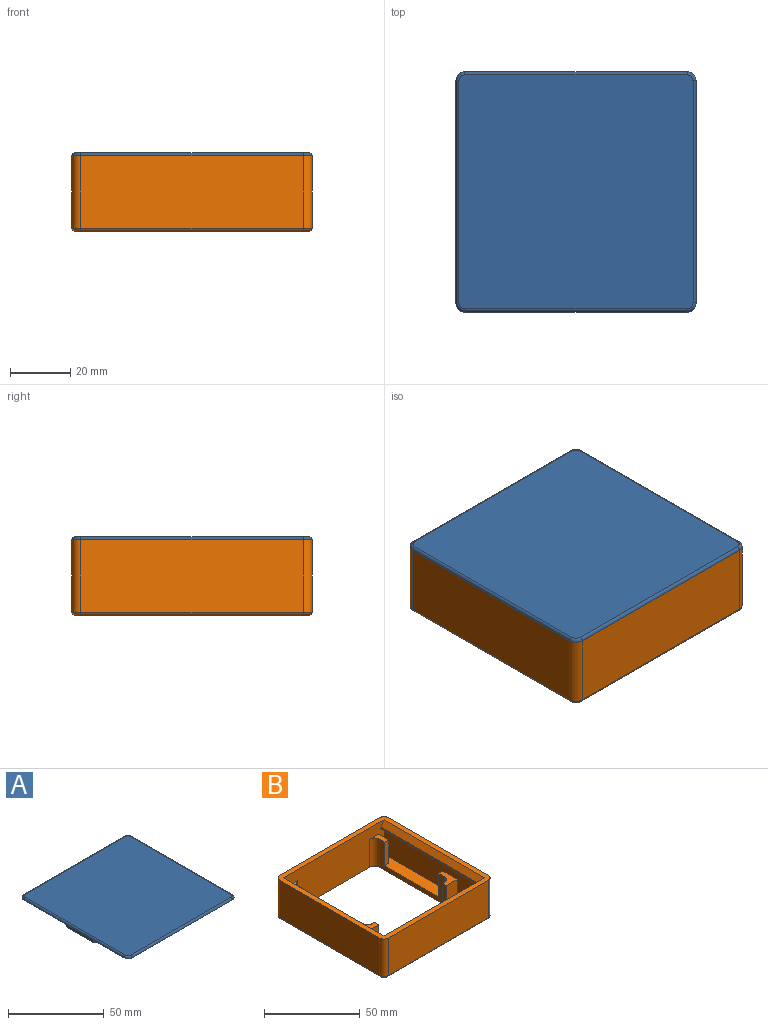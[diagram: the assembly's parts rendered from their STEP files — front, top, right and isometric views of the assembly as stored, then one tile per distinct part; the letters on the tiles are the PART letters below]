
ASSEMBLY  parts=2 mates=1
PART A: 46 faces, bbox 80.5x80.5x7.6 mm
  f0: plane 6.56x4.98mm, normal (0,-1,0), area 16.5mm2, adj f10,f30,f31,f32,f33,f35,f45
  f1: plane 6.56x4.98mm, normal (0,1,0), area 16.5mm2, adj f10,f30,f31,f32,f33,f35,f45
  f2: plane 5x3.12mm, normal (0,-1,0), area 11.7mm2, adj f10,f11,f22,f23
  f3: plane 3.12x2.5mm, normal (1,0,0), area 7.8mm2, adj f7,f8,f10,f20
  f4: plane 3.12x2.5mm, normal (-1,0,0), area 7.8mm2, adj f10,f12,f13,f19
  f5: plane 5x3.12mm, normal (0,-1,0), area 11.7mm2, adj f10,f14,f16,f17
  f6: plane 5x3.12mm, normal (0,1,0), area 11.7mm2, adj f10,f11,f22,f23
  f7: plane 5x3.12mm, normal (0,1,0), area 11.7mm2, adj f3,f10,f20,f21
  f8: plane 5x3.12mm, normal (0,-1,0), area 11.7mm2, adj f3,f10,f20,f21
  f9: plane 78x78mm, normal (0,0,1), area 6080.6mm2, adj f36,f37,f38,f39,f40,f41,f42,f43
  f10: plane 80x80mm, normal (0,0,-1), area 6193mm2, adj f0,f1,f2,f3,f4,f5,f6,f7
  f11: plane 3.12x2.5mm, normal (1,0,0), area 7.8mm2, adj f2,f6,f10,f23
  f12: plane 5x3.12mm, normal (0,1,0), area 11.7mm2, adj f4,f10,f18,f19
  f13: plane 5x3.12mm, normal (0,-1,0), area 11.7mm2, adj f4,f10,f18,f19
  f14: plane 3.12x2.5mm, normal (-1,0,0), area 7.8mm2, adj f5,f10,f15,f16
  f15: plane 5x3.12mm, normal (0,1,0), area 11.7mm2, adj f10,f14,f16,f17
  f16: plane 2.5x2.5mm, normal (0,0,-1), area 6.3mm2, adj f5,f14,f15,f17
  f17: plane 3.12x2.5mm, normal (0.78,0,-0.62), area 10mm2, adj f5,f10,f15,f16
  f18: plane 3.12x2.5mm, normal (0.78,0,-0.62), area 10mm2, adj f10,f12,f13,f19
  f19: plane 2.5x2.5mm, normal (0,0,-1), area 6.3mm2, adj f4,f12,f13,f18
  f20: plane 2.5x2.5mm, normal (0,0,-1), area 6.3mm2, adj f3,f7,f8,f21
  f21: plane 3.12x2.5mm, normal (-0.78,0,-0.62), area 10mm2, adj f7,f8,f10,f20
  f22: plane 3.12x2.5mm, normal (-0.78,0,-0.62), area 10mm2, adj f2,f6,f10,f23
  f23: plane 2.5x2.5mm, normal (0,0,-1), area 6.3mm2, adj f2,f6,f11,f22
  f24: plane 6.56x4.98mm, normal (0,-1,0), area 16.5mm2, adj f10,f26,f27,f28,f29,f34,f44
  f25: plane 6.56x4.98mm, normal (0,1,0), area 16.5mm2, adj f10,f26,f27,f28,f29,f34,f44
  f26: plane 20x0.57mm, normal (0.75,0,-0.66), area 15.1mm2, adj f24,f25,f29,f34
  f27: plane 20x4.3mm, normal (1,0,0), area 86mm2, adj f10,f24,f25,f28
  f28: plane 20x1.25mm, normal (0.27,0,0.96), area 26mm2, adj f24,f25,f27,f29
  f29: plane 20x1mm, normal (1,0,0), area 20mm2, adj f24,f25,f26,f28
  f30: plane 20x0.57mm, normal (-0.75,0,-0.66), area 15.1mm2, adj f0,f1,f31,f35
  f31: plane 20x1mm, normal (-1,0,0), area 20mm2, adj f0,f1,f30,f32
  f32: plane 20x1.25mm, normal (-0.27,0,0.96), area 26mm2, adj f0,f1,f31,f33
  f33: plane 20x4.3mm, normal (-1,0,0), area 86mm2, adj f0,f1,f10,f32
  f34: cylinder r=1mm len=20mm, axis (0,-1,0), area 41.1mm2, adj f24,f25,f26,f44
  f35: cylinder r=1mm len=20mm, axis (0,-1,0), area 41.1mm2, adj f0,f1,f30,f45
  f36: cylinder r=1mm len=74mm, axis (-1,0,0), area 116.2mm2, adj f9,f10,f37,f38
  f37: torus R=2mm, axis (0,0,1), area 6.5mm2, adj f9,f10,f36,f39
  f38: torus R=2mm, axis (0,0,1), area 6.5mm2, adj f9,f10,f36,f40
  f39: cylinder r=1mm len=74mm, axis (0,1,0), area 116.2mm2, adj f9,f10,f37,f41
  f40: cylinder r=1mm len=74mm, axis (0,-1,0), area 116.2mm2, adj f9,f10,f38,f42
  f41: torus R=2mm, axis (0,0,1), area 6.5mm2, adj f9,f10,f39,f43
  f42: torus R=2mm, axis (0,0,1), area 6.5mm2, adj f9,f10,f40,f43
  f43: cylinder r=1mm len=74mm, axis (1,0,0), area 116.2mm2, adj f9,f10,f41,f42
  f44: plane 20x5.92mm, normal (-0.9,0,-0.43), area 131mm2, adj f10,f24,f25,f34
  f45: plane 20x5.92mm, normal (0.9,0,-0.43), area 131mm2, adj f0,f1,f10,f35
PART B: 52 faces, bbox 80.5x80.5x25 mm
  f0: plane 74x25mm, normal (0,-1,0), area 1576.6mm2, adj f2,f3,f4,f5,f6,f7,f8,f18
  f1: plane 74x22mm, normal (0,1,0), area 1612.6mm2, adj f2,f31,f32,f33,f38,f39,f40,f41
  f2: plane 74x74mm, normal (0,0,1), area 2038mm2, adj f0,f1,f3,f4,f9,f11,f17,f19
  f3: plane 15x7.5mm, normal (1,0,0), area 112.5mm2, adj f0,f2,f5,f19
  f4: plane 15x7.5mm, normal (-1,0,0), area 112.5mm2, adj f0,f2,f6,f20
  f5: plane 7.5x6.5mm, normal (0,0,1), area 25.1mm2, adj f0,f3,f8,f9,f19
  f6: plane 7.5x6.5mm, normal (0,0,1), area 25.1mm2, adj f0,f4,f7,f17,f20
  f7: cylinder r=3.5mm len=18mm, axis (0,0,-1), area 99mm2, adj f0,f6,f17,f18
  f8: cylinder r=3.5mm len=18mm, axis (0,0,-1), area 99mm2, adj f0,f5,f9,f18
  f9: plane 48x18mm, normal (-1,0,0), area 264mm2, adj f2,f5,f8,f10,f18,f19,f24,f25
  f10: cylinder r=3.5mm len=18mm, axis (0,0,-1), area 99mm2, adj f9,f11,f18,f25
  f11: plane 53x18mm, normal (0,1,0), area 204mm2, adj f2,f10,f12,f18,f21,f25,f29,f30
  f12: cylinder r=3.5mm len=18mm, axis (0,0,-1), area 99mm2, adj f11,f17,f18,f30
  f13: plane 74x24mm, normal (1,0,0), area 1776mm2, adj f33,f36,f37,f48
  f14: plane 74x24mm, normal (0,1,0), area 1776mm2, adj f33,f34,f37,f51
  f15: plane 74x24mm, normal (-1,0,0), area 1776mm2, adj f33,f34,f35,f47
  f16: plane 74x24mm, normal (0,-1,0), area 1776mm2, adj f33,f35,f36,f44
  f17: plane 48x18mm, normal (1,0,0), area 264mm2, adj f2,f6,f7,f12,f18,f20,f26,f30
  f18: plane 78x78mm, normal (0,0,-1), area 2791.1mm2, adj f0,f7,f8,f9,f10,f11,f12,f17
  f19: plane 15x3mm, normal (0,-1,0), area 45mm2, adj f2,f3,f5,f9
  f20: plane 15x3mm, normal (0,-1,0), area 45mm2, adj f2,f4,f6,f17
  f21: plane 15x3mm, normal (-1,0,0), area 45mm2, adj f2,f11,f22,f25
  f22: plane 15x8mm, normal (0,-1,0), area 120mm2, adj f2,f21,f23,f25
  f23: plane 15x10.5mm, normal (1,0,0), area 157.5mm2, adj f2,f22,f24,f25
  f24: plane 15x3mm, normal (0,1,0), area 45mm2, adj f2,f9,f23,f25
  f25: plane 10.5x8mm, normal (0,0,1), area 49.1mm2, adj f9,f10,f11,f21,f22,f23,f24
  f26: plane 15x3mm, normal (0,1,0), area 45mm2, adj f2,f17,f27,f30
  f27: plane 15x10.5mm, normal (-1,0,0), area 157.5mm2, adj f2,f26,f28,f30
  f28: plane 15x8mm, normal (0,-1,0), area 120mm2, adj f2,f27,f29,f30
  f29: plane 15x3mm, normal (1,0,0), area 45mm2, adj f2,f11,f28,f30
  f30: plane 10.5x8mm, normal (0,0,1), area 49.1mm2, adj f11,f12,f17,f26,f27,f28,f29
  f31: plane 74x17mm, normal (-1,0,0), area 1258mm2, adj f0,f1,f2,f41
  f32: plane 74x17mm, normal (1,0,0), area 1258mm2, adj f0,f1,f2,f40
  f33: plane 80x80mm, normal (0,0,1), area 916.3mm2, adj f0,f1,f13,f14,f15,f16,f34,f35
  f34: cylinder r=3mm len=24mm, axis (0,0,1), area 113.1mm2, adj f14,f15,f33,f49
  f35: cylinder r=3mm len=24mm, axis (0,0,-1), area 113.1mm2, adj f15,f16,f33,f45
  f36: cylinder r=3mm len=24mm, axis (0,0,1), area 113.1mm2, adj f13,f16,f33,f46
  f37: cylinder r=3mm len=24mm, axis (0,0,-1), area 113.1mm2, adj f13,f14,f33,f50
  f38: plane 74x3.12mm, normal (0.78,0,0.62), area 296mm2, adj f0,f1,f33,f39
  f39: plane 74x1.16mm, normal (1,0,0), area 86.1mm2, adj f0,f1,f38,f40
  f40: plane 74x2.5mm, normal (0.27,0,-0.96), area 192.4mm2, adj f0,f1,f32,f39
  f41: plane 74x2.5mm, normal (-0.27,0,-0.96), area 192.4mm2, adj f0,f1,f31,f42
  f42: plane 74x1.16mm, normal (-1,0,0), area 86.1mm2, adj f0,f1,f41,f43
  f43: plane 74x3.12mm, normal (-0.78,0,0.62), area 296mm2, adj f0,f1,f33,f42
  f44: cylinder r=1mm len=74mm, axis (1,0,0), area 116.2mm2, adj f16,f18,f45,f46
  f45: torus R=2mm, axis (0,0,1), area 6.5mm2, adj f18,f35,f44,f47
  f46: torus R=2mm, axis (0,0,1), area 6.5mm2, adj f18,f36,f44,f48
  f47: cylinder r=1mm len=74mm, axis (0,-1,0), area 116.2mm2, adj f15,f18,f45,f49
  f48: cylinder r=1mm len=74mm, axis (0,1,0), area 116.2mm2, adj f13,f18,f46,f50
  f49: torus R=2mm, axis (0,0,1), area 6.5mm2, adj f18,f34,f47,f51
  f50: torus R=2mm, axis (0,0,1), area 6.5mm2, adj f18,f37,f48,f51
  f51: cylinder r=1mm len=74mm, axis (-1,0,0), area 116.2mm2, adj f14,f18,f49,f50
PLACE A at identity
PLACE B t=(0,0,25)mm
MATE fastened B.f35 <-> A.f37  axis (0,0,1) through (-77,3,50)mm
